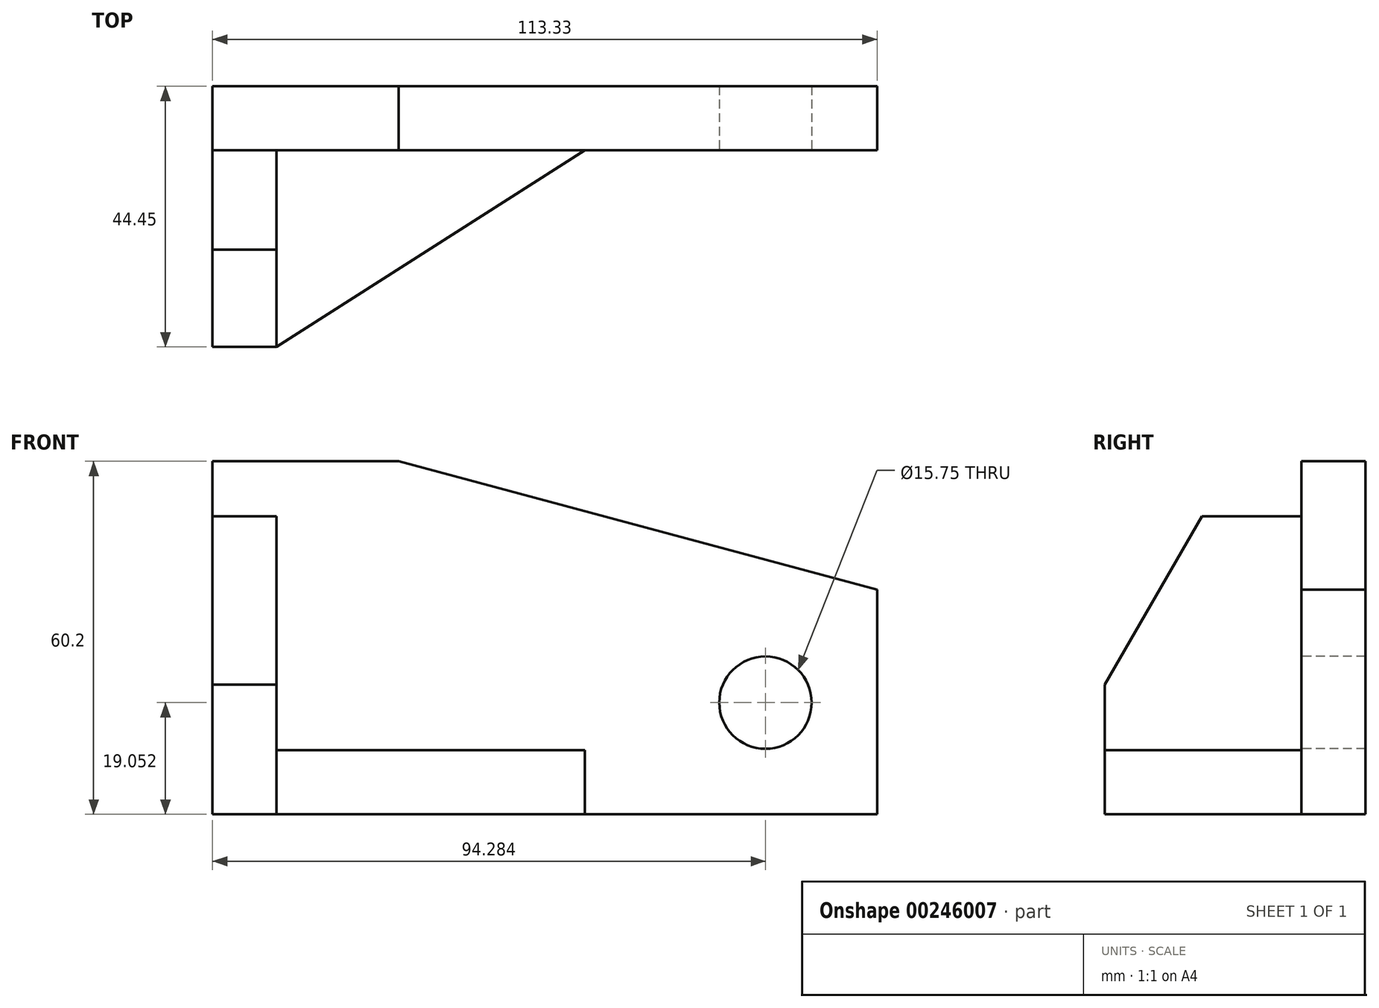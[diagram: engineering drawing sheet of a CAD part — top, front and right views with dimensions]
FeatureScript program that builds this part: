
annotation { "Feature Type Name" : "Feature", "Feature Type Description" : "" }
export const myFeature = defineFeature(function(context is Context, id is Id, definition is map)
    precondition{}
    {
        {
            var Q0;
            Q0=qCreatedBy(makeId("Front.planeOp"),FACE);
            var sketch = newSketch(context, id + "F0", { "sketchPlane" : qUnion([Q0])});
            skLineSegment(sketch, "E0.bottom", {"start": v(-39.45, 38.1) * mm, "end": v(-7.7, 38.1) * mm});
            skLineSegment(sketch, "E0.top", {"start": v(-39.45, -22.1) * mm, "end": v(-7.7, -22.1) * mm});
            skLineSegment(sketch, "E0.left", {"start": v(-39.45, 38.1) * mm, "end": v(-39.45, -22.1) * mm});
            skLineSegment(sketch, "E0.right", {"start": v(-7.7, 38.1) * mm, "end": v(-7.7, -22.1) * mm});
            skLineSegment(sketch, "E1.bottom", {"start": v(-7.7, 38.1) * mm, "end": v(73.88, 16.24) * mm});
            skLineSegment(sketch, "E1.top", {"start": v(-7.7, -22.1) * mm, "end": v(73.88, -22.1) * mm});
            skLineSegment(sketch, "E1.right", {"start": v(73.88, 16.24) * mm, "end": v(73.88, -22.1) * mm});
            skCircle(sketch, "E2", {"center": v(54.83, -3.05) * mm, "radius": 7.87 * mm});
            skLineSegment(sketch, "E3.top", {"start": v(-39.45, 28.7) * mm, "end": v(-28.53, 28.7) * mm});
            skLineSegment(sketch, "E3.right", {"start": v(-28.53, -22.1) * mm, "end": v(-28.53, 28.7) * mm});
            skLineSegment(sketch, "E4", {"start": v(-39.45, 0) * mm, "end": v(-28.53, 0) * mm});
            skSolve(sketch);
        }
        {
            var Q0;
            {var subQ5=sQuery(id+"F0.wireOp",EDGE,"E0.bottom");Q0=makeQuery(id+"F0.imprint","IMPRINT",FACE,{"disambiguationData":[TD([[makeQuery(id+"F0.imprint","IMPRINT",EDGE,{"derivedFrom":subQ5}),-1.0]])]});}
            var Q1;
            Q1=makeQuery(id+"F0.imprint","IMPRINT",FACE,{"disambiguationData":[TD([[makeQuery(id+"F0.imprint","IMPRINT",EDGE,{"derivedFrom":sQuery(id+"F0.wireOp",EDGE,"E0.right")}),1.0]])]});
            var Q2;
            {var subQ5=sQuery(id+"F0.wireOp",EDGE,"E4");Q2=makeQuery(id+"F0.imprint","IMPRINT",FACE,{"disambiguationData":[TD([[makeQuery(id+"F0.imprint","IMPRINT",EDGE,{"derivedFrom":subQ5}),-1.0]])]});}
            var Q3;
            {var subQ0=sQuery(id+"F0.wireOp",EDGE,"E3.top");Q3=makeQuery(id+"F0.imprint","IMPRINT",FACE,{"disambiguationData":[TD([[makeQuery(id+"F0.imprint","IMPRINT",EDGE,{"derivedFrom":subQ0}),-1.0]])]});}
            extrude(context, id + "F1", {"entities" : qUnion([Q0, Q1, Q2, Q3]), "oppositeDirection" : true, "depth" : 10.92 * mm});
        }
        {
            var Q0;
            {var subQ0=sQuery(id+"F0.wireOp",EDGE,"E3.top");Q0=makeQuery(id+"F0.imprint","IMPRINT",FACE,{"disambiguationData":[TD([[makeQuery(id+"F0.imprint","IMPRINT",EDGE,{"derivedFrom":subQ0}),-1.0]])]});}
            var Q1;
            {var subQ5=sQuery(id+"F0.wireOp",EDGE,"E4");Q1=makeQuery(id+"F0.imprint","IMPRINT",FACE,{"disambiguationData":[TD([[makeQuery(id+"F0.imprint","IMPRINT",EDGE,{"derivedFrom":subQ5}),-1.0]])]});}
            extrude(context, id + "F2", {"entities" : qUnion([Q0, Q1]), "operationType" : NewBodyOperationType.ADD, "depth" : 33.53 * mm});
        }
        {
            var Q0;
            Q0=makeQuery(id+"F2.opExtrude","SWEPT_FACE",FACE,{"disambiguationData":[OSD([sQuery(id+"F0.wireOp",EDGE,"E3.right")])]});
            var sketch = newSketch(context, id + "F3", { "sketchPlane" : qUnion([Q0])});
            skLineSegment(sketch, "E5", {"start": v(-33.53, 0) * mm, "end": v(-16.96, 28.7) * mm});
            skLineSegment(sketch, "E6", {"start": v(-33.53, -11.18) * mm, "end": v(0, -11.18) * mm});
            skSolve(sketch);
        }
        {
            var Q0;
            {var subQ1=sQuery(id+"F0.wireOp",EDGE,"E3.right");var subQ6=makeQuery(id+"F2.opExtrude","SWEPT_EDGE",EDGE,{"disambiguationData":[OSD([sQuery(id+"F0.wireOp",EDGE,"E3.top"),subQ1])]});Q0=makeQuery(id+"F3.imprint","IMPRINT",FACE,{"disambiguationData":[TD([[makeQuery(id+"F3.imprint","IMPRINT",EDGE,{"derivedFrom":subQ6}),-1.0]])]});}
            extrude(context, id + "F4", {"entities" : qUnion([Q0]), "operationType" : NewBodyOperationType.REMOVE, "oppositeDirection" : true, "depth" : 25.4 * mm});
        }
        {
            var Q0;
            {var subQ0=sQuery(id+"F3.wireOp",EDGE,"E6");Q0=makeQuery(id+"F3.imprint","IMPRINT",FACE,{"disambiguationData":[TD([[makeQuery(id+"F3.imprint","IMPRINT",EDGE,{"derivedFrom":subQ0}),-1.0]])]});}
            extrude(context, id + "F5", {"entities" : qUnion([Q0]), "operationType" : NewBodyOperationType.ADD, "depth" : 52.58 * mm});
        }
        {
            var Q0;
            Q0=makeQuery(id+"F5.opExtrude","SWEPT_FACE",FACE,{"disambiguationData":[OSD([sQuery(id+"F3.wireOp",EDGE,"E6")])]});
            var sketch = newSketch(context, id + "F6", { "sketchPlane" : qUnion([Q0])});
            skLineSegment(sketch, "E7", {"start": v(-28.53, -33.53) * mm, "end": v(24.05, 0) * mm});
            skSolve(sketch);
        }
        {
            var Q0;
            Q0=makeQuery(id+"F6.imprint","IMPRINT",FACE,{"disambiguationData":[TD([[makeQuery(id+"F6.imprint","IMPRINT",EDGE,{"derivedFrom":sQuery(id+"F6.wireOp",EDGE,"E7")}),-1.0]])]});
            extrude(context, id + "F7", {"entities" : qUnion([Q0]), "operationType" : NewBodyOperationType.REMOVE, "oppositeDirection" : true, "depth" : 25.4 * mm});
        }
    });
